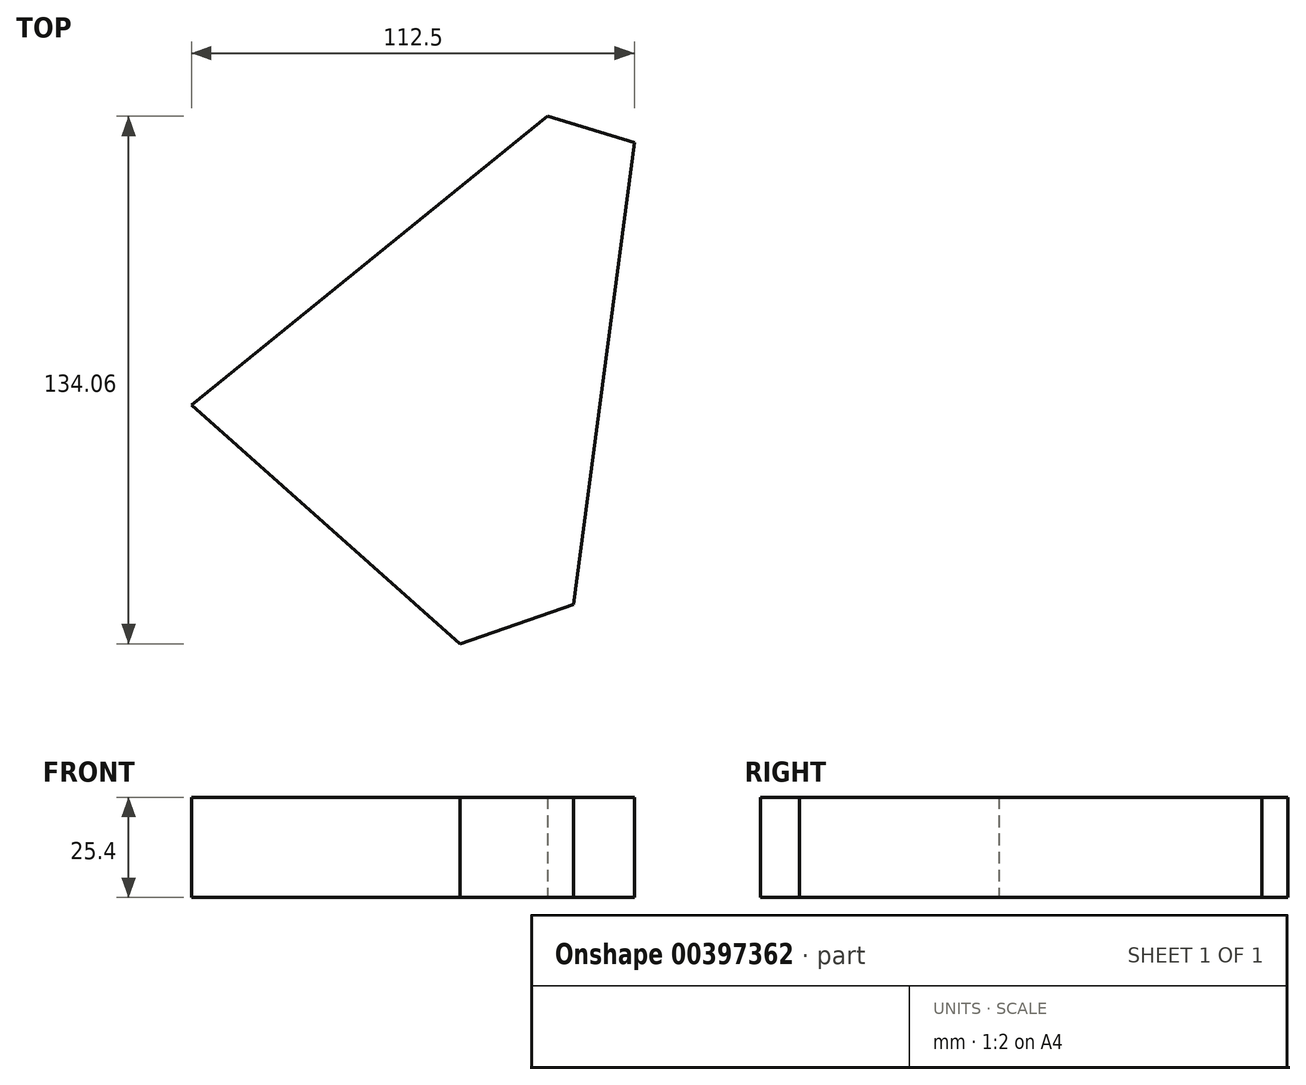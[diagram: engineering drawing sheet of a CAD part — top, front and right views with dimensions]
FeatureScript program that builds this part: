
annotation { "Feature Type Name" : "Feature", "Feature Type Description" : "" }
export const myFeature = defineFeature(function(context is Context, id is Id, definition is map)
    precondition{}
    {
        {
            var Q0;
            Q0=qCreatedBy(makeId("Top.planeOp"),FACE);
            var sketch = newSketch(context, id + "F0", { "sketchPlane" : qUnion([Q0])});
            skLineSegment(sketch, "E0", {"start": v(0.27, -70.87) * mm, "end": v(-67.97, -10.19) * mm});
            skLineSegment(sketch, "E1", {"start": v(-67.97, -10.19) * mm, "end": v(22.52, 63.2) * mm});
            skLineSegment(sketch, "E2", {"start": v(22.52, 63.2) * mm, "end": v(44.53, 56.5) * mm});
            skLineSegment(sketch, "E3", {"start": v(0.27, -70.87) * mm, "end": v(29.04, -60.93) * mm});
            skLineSegment(sketch, "E4", {"start": v(29.04, -60.93) * mm, "end": v(44.53, 56.5) * mm});
            skLineSegment(sketch, "E5", {"start": v(30.17, -52.37) * mm, "end": v(-10.9, -60.93) * mm});
            skLineSegment(sketch, "E6", {"start": v(31.75, -40.38) * mm, "end": v(-21.53, -51.48) * mm});
            skLineSegment(sketch, "E7", {"start": v(33.38, -28.02) * mm, "end": v(-28.58, -40.93) * mm});
            skLineSegment(sketch, "E8", {"start": v(32.09, -13.18) * mm, "end": v(-46.25, -29.5) * mm});
            skLineSegment(sketch, "E9", {"start": v(36.79, -2.2) * mm, "end": v(-64.36, -18.32) * mm});
            skLineSegment(sketch, "E10", {"start": v(37.58, 3.8) * mm, "end": v(-60.57, -4.19) * mm});
            skLineSegment(sketch, "E11", {"start": v(38.73, 12.56) * mm, "end": v(-35.42, 16.21) * mm});
            skLineSegment(sketch, "E12", {"start": v(40.02, 22.3) * mm, "end": v(-22.73, 26.5) * mm});
            skLineSegment(sketch, "E13", {"start": v(41.15, 30.93) * mm, "end": v(-10.9, 34.41) * mm});
            skLineSegment(sketch, "E14", {"start": v(42.75, 43.05) * mm, "end": v(0.27, 45.9) * mm});
            skLineSegment(sketch, "E15", {"start": v(40.36, 49.99) * mm, "end": v(14.27, 56.5) * mm});
            skSolve(sketch);
        }
        {
            var Q0;
            Q0 = qSketchRegion(id + "F0", true);
            extrude(context, id + "F1", {"entities" : qUnion([Q0]), "depth" : 25.4 * mm});
        }
        {
            var Q0;
            Q0=makeQuery(id+"F1.opExtrude","CAP_FACE",FACE,{"disambiguationData":[OSD([sQuery(id+"F0.wireOp",EDGE,"E0"),sQuery(id+"F0.wireOp",EDGE,"E1"),sQuery(id+"F0.wireOp",EDGE,"E2"),sQuery(id+"F0.wireOp",EDGE,"E3"),sQuery(id+"F0.wireOp",EDGE,"E4")])],"isStart":true});
            var sketch = newSketch(context, id + "F2", { "sketchPlane" : qUnion([Q0])});
            skLineSegment(sketch, "E16", {"start": v(29.58, 56.9) * mm, "end": v(-5.66, 65.6) * mm});
            skLineSegment(sketch, "E17", {"start": v(31.12, 45.2) * mm, "end": v(-10.9, 60.93) * mm});
            skLineSegment(sketch, "E18", {"start": v(32.72, 33.07) * mm, "end": v(-15.97, 51.03) * mm});
            skLineSegment(sketch, "E19", {"start": v(33.8, 24.89) * mm, "end": v(-31.1, 42.98) * mm});
            skLineSegment(sketch, "E20", {"start": v(35.14, 14.7) * mm, "end": v(-40.8, 34.34) * mm});
            skLineSegment(sketch, "E21", {"start": v(36.79, 2.2) * mm, "end": v(-50.77, 25.48) * mm});
            skLineSegment(sketch, "E22", {"start": v(37.7, -4.78) * mm, "end": v(-67.97, 10.19) * mm});
            skLineSegment(sketch, "E23", {"start": v(38.4, -10.03) * mm, "end": v(-43.04, -10.03) * mm});
            skLineSegment(sketch, "E24", {"start": v(39.83, -20.92) * mm, "end": v(-28.49, -26.5) * mm});
            skPoint(sketch, "E24.endSnap0", {"position": v(-22.73, -26.5) * mm});
            skLineSegment(sketch, "E25", {"start": v(41.25, -31.68) * mm, "end": v(-4.93, -40.94) * mm});
            skLineSegment(sketch, "E26", {"start": v(43.1, -45.72) * mm, "end": v(6.86, -50.5) * mm});
            skSolve(sketch);
        }
        {
            var Q0;
            {var subQ0=sQuery(id+"F2.wireOp",EDGE,"E16");Q0=makeQuery(id+"F2.imprint","IMPRINT",FACE,{"disambiguationData":[TD([[makeQuery(id+"F2.imprint","IMPRINT",EDGE,{"derivedFrom":subQ0}),-1.0]])]});}
            var Q1;
            {var subQ0=sQuery(id+"F2.wireOp",EDGE,"E16");Q1=makeQuery(id+"F2.imprint","IMPRINT",FACE,{"disambiguationData":[TD([[makeQuery(id+"F2.imprint","IMPRINT",EDGE,{"derivedFrom":subQ0}),1.0]])]});}
            var Q2;
            {var subQ0=sQuery(id+"F2.wireOp",EDGE,"E17");Q2=makeQuery(id+"F2.imprint","IMPRINT",FACE,{"disambiguationData":[TD([[makeQuery(id+"F2.imprint","IMPRINT",EDGE,{"derivedFrom":subQ0}),1.0]])]});}
            var Q3;
            {var subQ0=sQuery(id+"F2.wireOp",EDGE,"E19");Q3=makeQuery(id+"F2.imprint","IMPRINT",FACE,{"disambiguationData":[TD([[makeQuery(id+"F2.imprint","IMPRINT",EDGE,{"derivedFrom":subQ0}),1.0]])]});}
            var Q4;
            {var subQ0=sQuery(id+"F2.wireOp",EDGE,"E22");Q4=makeQuery(id+"F2.imprint","IMPRINT",FACE,{"disambiguationData":[TD([[makeQuery(id+"F2.imprint","IMPRINT",EDGE,{"derivedFrom":subQ0}),1.0]])]});}
            var Q5;
            {var subQ0=sQuery(id+"F2.wireOp",EDGE,"E23");Q5=makeQuery(id+"F2.imprint","IMPRINT",FACE,{"disambiguationData":[TD([[makeQuery(id+"F2.imprint","IMPRINT",EDGE,{"derivedFrom":subQ0}),1.0]])]});}
            var Q6;
            {var subQ5=sQuery(id+"F2.wireOp",EDGE,"E25");Q6=makeQuery(id+"F2.imprint","IMPRINT",FACE,{"disambiguationData":[TD([[makeQuery(id+"F2.imprint","IMPRINT",EDGE,{"derivedFrom":subQ5}),-1.0]])]});}
            var Q7;
            {var subQ0=sQuery(id+"F2.wireOp",EDGE,"E21");Q7=makeQuery(id+"F2.imprint","IMPRINT",FACE,{"disambiguationData":[TD([[makeQuery(id+"F2.imprint","IMPRINT",EDGE,{"derivedFrom":subQ0}),1.0]])]});}
            var Q8;
            {var subQ0=sQuery(id+"F2.wireOp",EDGE,"E20");Q8=makeQuery(id+"F2.imprint","IMPRINT",FACE,{"disambiguationData":[TD([[makeQuery(id+"F2.imprint","IMPRINT",EDGE,{"derivedFrom":subQ0}),1.0]])]});}
            var Q9;
            {var subQ0=sQuery(id+"F2.wireOp",EDGE,"E25");Q9=makeQuery(id+"F2.imprint","IMPRINT",FACE,{"disambiguationData":[TD([[makeQuery(id+"F2.imprint","IMPRINT",EDGE,{"derivedFrom":subQ0}),1.0]])]});}
            var Q10;
            {var subQ0=sQuery(id+"F2.wireOp",EDGE,"E26");Q10=makeQuery(id+"F2.imprint","IMPRINT",FACE,{"disambiguationData":[TD([[makeQuery(id+"F2.imprint","IMPRINT",EDGE,{"derivedFrom":subQ0}),1.0]])]});}
            extrude(context, id + "F3", {"entities" : qUnion([Q0, Q1, Q2, Q3, Q4, Q5, Q6, Q7, Q8, Q9, Q10]), "operationType" : NewBodyOperationType.ADD, "oppositeDirection" : true, "depth" : 12.45 * mm});
        }
    });
